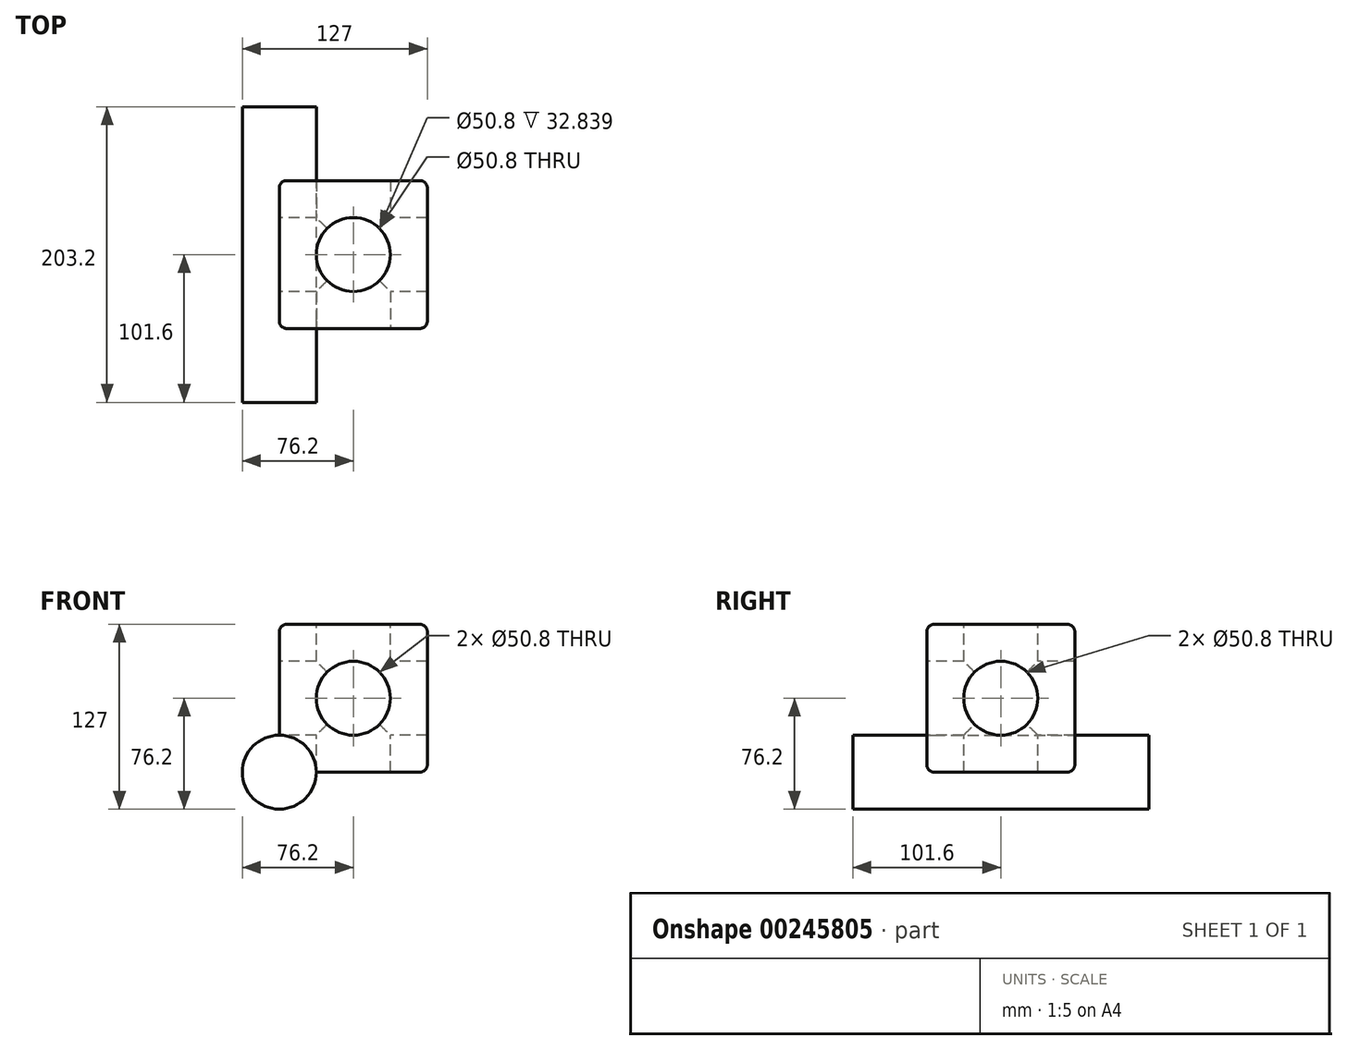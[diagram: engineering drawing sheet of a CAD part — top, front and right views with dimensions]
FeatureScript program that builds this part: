
annotation { "Feature Type Name" : "Feature", "Feature Type Description" : "" }
export const myFeature = defineFeature(function(context is Context, id is Id, definition is map)
    precondition{}
    {
        {
            var Q0;
            Q0=qCreatedBy(makeId("Front.planeOp"),FACE);
            var sketch = newSketch(context, id + "F0", { "sketchPlane" : qUnion([Q0])});
            skLineSegment(sketch, "E0", {"start": v(0, 0) * mm, "end": v(101.6, 0) * mm});
            skLineSegment(sketch, "E1", {"start": v(101.6, 0) * mm, "end": v(101.6, 101.6) * mm});
            skLineSegment(sketch, "E2", {"start": v(101.6, 101.6) * mm, "end": v(0, 101.6) * mm});
            skLineSegment(sketch, "E3", {"start": v(0, 101.6) * mm, "end": v(0, 0) * mm});
            skSolve(sketch);
        }
        {
            var Q0;
            Q0=makeQuery(id+"F0.imprint","IMPRINT",FACE,{"disambiguationData":[TD([[makeQuery(id+"F0.imprint","IMPRINT",EDGE,{"derivedFrom":sQuery(id+"F0.wireOp",EDGE,"E0")}),1.0]])]});
            extrude(context, id + "F1", {"entities" : qUnion([Q0]), "depth" : 101.6 * mm});
        }
        {
            var Q0;
            Q0=makeQuery(id+"F1.opExtrude","CAP_FACE",FACE,{"disambiguationData":[OSD([sQuery(id+"F0.wireOp",EDGE,"E0"),sQuery(id+"F0.wireOp",EDGE,"E1"),sQuery(id+"F0.wireOp",EDGE,"E2"),sQuery(id+"F0.wireOp",EDGE,"E3")])],"isStart":false});
            var sketch = newSketch(context, id + "F2", { "sketchPlane" : qUnion([Q0])});
            skLineSegment(sketch, "E4", {"start": v(50.8, 101.6) * mm, "end": v(50.8, 0) * mm});
            skCircle(sketch, "E5", {"center": v(50.8, 50.8) * mm, "radius": 25.4 * mm});
            skSolve(sketch);
        }
        {
            var Q0;
            Q0 = qSketchRegion(id + "F2", true);
            extrude(context, id + "F3", {"entities" : qUnion([Q0]), "operationType" : NewBodyOperationType.REMOVE, "oppositeDirection" : true, "depth" : 101.6 * mm});
        }
        {
            var Q0;
            Q0=makeQuery(id+"F1.opExtrude","SWEPT_FACE",FACE,{"disambiguationData":[OSD([sQuery(id+"F0.wireOp",EDGE,"E3")])]});
            var sketch = newSketch(context, id + "F4", { "sketchPlane" : qUnion([Q0])});
            skLineSegment(sketch, "E6", {"start": v(50.8, 101.6) * mm, "end": v(50.8, 0) * mm});
            skCircle(sketch, "E7", {"center": v(50.8, 50.8) * mm, "radius": 25.4 * mm});
            skSolve(sketch);
        }
        {
            var Q0;
            Q0 = qSketchRegion(id + "F4", true);
            extrude(context, id + "F5", {"entities" : qUnion([Q0]), "operationType" : NewBodyOperationType.REMOVE, "oppositeDirection" : true, "depth" : 101.6 * mm});
        }
        {
            var Q0;
            Q0=makeQuery(id+"F1.opExtrude","SWEPT_FACE",FACE,{"disambiguationData":[OSD([sQuery(id+"F0.wireOp",EDGE,"E2")])]});
            var sketch = newSketch(context, id + "F6", { "sketchPlane" : qUnion([Q0])});
            skLineSegment(sketch, "E8", {"start": v(50.8, -101.6) * mm, "end": v(50.8, 0) * mm});
            skCircle(sketch, "E9", {"center": v(50.8, -50.8) * mm, "radius": 25.4 * mm});
            skSolve(sketch);
        }
        {
            var Q0;
            Q0 = qSketchRegion(id + "F6", true);
            extrude(context, id + "F7", {"entities" : qUnion([Q0]), "operationType" : NewBodyOperationType.REMOVE, "oppositeDirection" : true, "depth" : 101.6 * mm});
        }
        {
            var Q0;
            Q0=qCreatedBy(makeId("Front.planeOp"),FACE);
            cPlane(context, id + "F8", {"entities" : qUnion([Q0]), "cplaneType" : CPlaneType.OFFSET, "offset" : 101.6 * mm, "width" : 152.4 * mm, "height" : 152.4 * mm});
        }
        {
            var Q0;
            Q0=qCreatedBy(id+"F8.planeOp",FACE);
            var sketch = newSketch(context, id + "F9", { "sketchPlane" : qUnion([Q0])});
            skCircle(sketch, "E10", {"center": v(0, 0) * mm, "radius": 25.4 * mm});
            skSolve(sketch);
        }
        {
            var Q0;
            Q0 = qSketchRegion(id + "F9", true);
            extrude(context, id + "F10", {"entities" : qUnion([Q0]), "operationType" : NewBodyOperationType.ADD, "depth" : 50.8 * mm, "hasSecondDirection" : true, "secondDirectionOppositeDirection" : true, "secondDirectionDepth" : 152.4 * mm});
        }
        {
            var Q0;
            Q0=makeQuery(id+"F1.opExtrude","CAP_EDGE",EDGE,{"disambiguationData":[OSD([sQuery(id+"F0.wireOp",EDGE,"E2")])],"isStart":false});
            var Q1;
            Q1=makeQuery(id+"F1.opExtrude","SWEPT_EDGE",EDGE,{"disambiguationData":[OSD([sQuery(id+"F0.wireOp",EDGE,"E1"),sQuery(id+"F0.wireOp",EDGE,"E2")])]});
            var Q2;
            Q2=makeQuery(id+"F1.opExtrude","CAP_EDGE",EDGE,{"disambiguationData":[OSD([sQuery(id+"F0.wireOp",EDGE,"E2")])],"isStart":true});
            var Q3;
            Q3=makeQuery(id+"F1.opExtrude","SWEPT_EDGE",EDGE,{"disambiguationData":[OSD([sQuery(id+"F0.wireOp",EDGE,"E2"),sQuery(id+"F0.wireOp",EDGE,"E3")])]});
            var Q4;
            Q4=makeQuery(id+"F1.opExtrude","CAP_EDGE",EDGE,{"disambiguationData":[OSD([sQuery(id+"F0.wireOp",EDGE,"E1")])],"isStart":false});
            var Q5;
            Q5=makeQuery(id+"F1.opExtrude","CAP_EDGE",EDGE,{"disambiguationData":[OSD([sQuery(id+"F0.wireOp",EDGE,"E1")])],"isStart":true});
            var Q6;
            Q6=makeQuery(id+"F1.opExtrude","SWEPT_EDGE",EDGE,{"disambiguationData":[OSD([sQuery(id+"F0.wireOp",EDGE,"E0"),sQuery(id+"F0.wireOp",EDGE,"E1")])]});
            var Q7;
            Q7=makeQuery(id+"F1.opExtrude","CAP_EDGE",EDGE,{"disambiguationData":[OSD([sQuery(id+"F0.wireOp",EDGE,"E3")])],"isStart":false});
            var Q8;
            Q8=makeQuery(id+"F1.opExtrude","CAP_EDGE",EDGE,{"disambiguationData":[OSD([sQuery(id+"F0.wireOp",EDGE,"E0")])],"isStart":false});
            var Q9;
            Q9=makeQuery(id+"F1.opExtrude","CAP_EDGE",EDGE,{"disambiguationData":[OSD([sQuery(id+"F0.wireOp",EDGE,"E0")])],"isStart":true});
            var Q10;
            Q10=makeQuery(id+"F1.opExtrude","CAP_EDGE",EDGE,{"disambiguationData":[OSD([sQuery(id+"F0.wireOp",EDGE,"E3")])],"isStart":true});
            fillet(context, id + "F11", {"entities" : qUnion([Q0, Q1, Q2, Q3, Q4, Q5, Q6, Q7, Q8, Q9, Q10]), "radius" : 5.08 * mm, "tangentPropagation" : true, "allowEdgeOverflow" : false});
        }
    });
